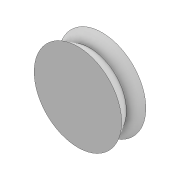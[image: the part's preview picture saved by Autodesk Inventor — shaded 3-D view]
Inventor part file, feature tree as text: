
AUTODESK INVENTOR PART (.ipt)
format: ipt  version: 2020 (Build 240168000, 168)  size: 98,816 bytes
history: native  units: mm
features: sketch x4, other x3, loft x2, extrude x1
ambient origin geometry x8: Origin, YZ Plane, XZ Plane, XY Plane, X Axis, Y Axis, Z Axis, Center Point
bodies: Body1 (feature_tree)
feature tree (10):
  sketch  "스케치1"
  other  "작업 평면2"
  sketch  "스케치2"
  other  "작업 평면1"
  loft  "로프트1"
  loft  "로프트2"
  extrude  "돌출2"  TaperAngle=0.0deg  [1 undecoded]
  sketch  "스케치3"
  other  "모서리1"
  sketch  "스케치4"
note: 1 required parameter value undecoded (feature->parameter linkage not recoverable at this tier; creation-order binding heuristic only, values carry confidence <= 0.55)
